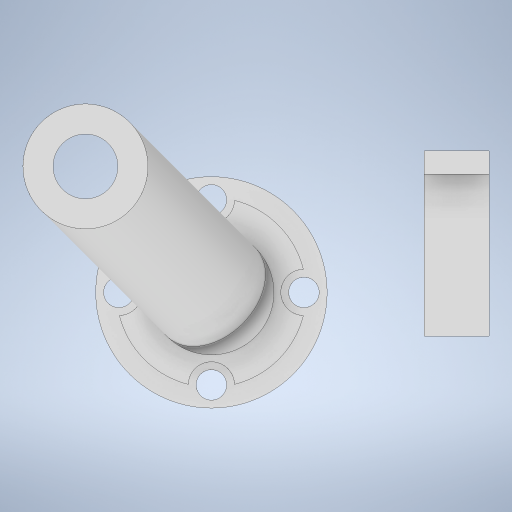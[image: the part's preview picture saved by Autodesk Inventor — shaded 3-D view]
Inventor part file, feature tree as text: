
AUTODESK INVENTOR PART (.ipt)
format: ipt  version: 2024 (Build 280153000, 153)  size: 394,752 bytes
history: native  units: mm
features: sketch x16, extrude x9, plane x4, other x2, hole x1, pattern_circular x1, split x1
ambient origin geometry x8: Origin, YZ Plane, XZ Plane, XY Plane, X Axis, Y Axis, Z Axis, Center Point
bodies: Body1 (feature_tree)
feature tree (34):
  other  "Sólido1"
  extrude  "Extrusión1"  Depth=6.0mm TaperAngle=0.0deg
  hole  "Agujero1"  [1 undecoded]
  extrude  "Extrusión2"  Depth=7.0mm
  other  "Empalme de cara1"
  sketch  "Boceto4"  dims[d19=40.0mm d20=0.0mm d21=7.0mm]
  extrude  "Extrusión3"  Depth=10.0mm TaperAngle=0.0deg
  pattern_circular  "Patrón circular1"  Count=4 Angle=360.0deg
  sketch  "Boceto16"  dims[d52=45.0deg d57=45.0deg]
  plane  "Plano de trabajo5"
  split  "Dividir2"
  sketch  "Boceto18"  dims[d58=90.0deg d59=38.5mm]
  plane  "Plano de trabajo6"
  sketch  "Boceto19"  dims[d60=135.0deg d63=0.0mm]
  sketch  "Boceto20"  dims[d64=13.5mm d65=18.0mm]
  plane  "Plano de trabajo7"
  extrude  "Extrusión6"  TaperAngle=45.0deg  [1 undecoded]
  extrude  "Extrusión7"  Depth=38.5mm
  extrude  "Extrusión8"  TaperAngle=0.0deg  [1 undecoded]
  sketch  "Boceto24"  dims[d73=7.0mm d74=0.0mm]
  plane  "Plano de trabajo8"
  extrude  "Extrusión9"  Depth=18.0mm
  extrude  "Extrusión10"  Depth=132.0mm
  extrude  "Extrusión11"  Depth=27.0mm
  sketch  "Boceto1"  dims[d0=50.0mm d7=6.0mm d8=0.0mm]
  sketch  "Boceto2"  dims[d9=40.0mm]
  sketch  "Boceto3"  dims[d10=6.6mm d11=0.5mm d12=12.6mm d13=2.0mm d14=90.0deg d15=8.0mm d16=20.594885mm d18=27.0mm]
  sketch  "Boceto5"  dims[d22=10.0mm d23=10.0mm d24=0.0mm d25=40.0mm d26=360.0deg]
  sketch  "Boceto21"  dims[d66=132.0mm d67=0.0mm d68=27.0mm]
  sketch  "Boceto22"  dims[d69=180.0mm d70=0.0mm d71=27.0mm]
  sketch  "Boceto23"  dims[d72=14.0mm]
  sketch  "Boceto25"  dims[d75=90.0deg]
  sketch  "Boceto27"  dims[d76=5.0mm]
  sketch  "Boceto29"  dims[d77=7.0mm d78=14.0mm d79=5.0mm d80=27.0mm d81=0.0mm d83=14.0mm d84=40.0mm d85=5.0mm d86=0.0mm d87=14.0mm d88=5.0mm d89=5.0mm d90=0.0mm d33=0.5mm d34=0.872665mm d35=0.5mm d36=0.872665mm d48=0.5mm d49=0.872665mm d50=0.5mm d51=0.872665mm]
note: 3 required parameter values undecoded (feature->parameter linkage not recoverable at this tier; creation-order binding heuristic only, values carry confidence <= 0.55)
